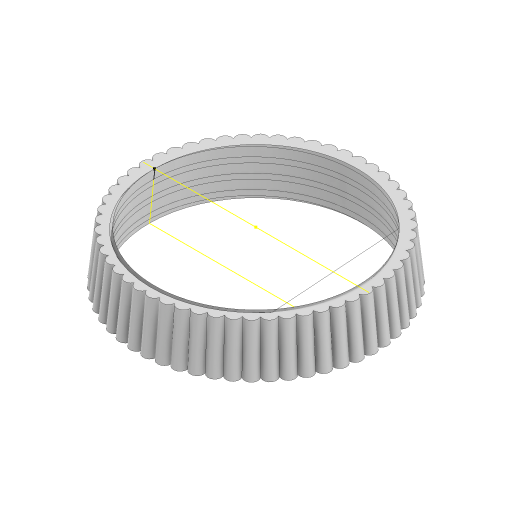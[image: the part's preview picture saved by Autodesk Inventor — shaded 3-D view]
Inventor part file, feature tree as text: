
AUTODESK INVENTOR PART (.ipt)
format: ipt  version: 2023 (Build 270158000, 158)  size: 462,336 bytes
history: native  units: mm
features: sketch x5, draft x2, helix x2, extrude x1, sweep x1, pattern_circular x1
ambient origin geometry x8: Origin, YZ Plane, XZ Plane, XY Plane, X Axis, Y Axis, Z Axis, Center Point
bodies: Solid1 (feature_tree)
feature tree (12):
  extrude  "Extrusion1"  Depth=6.52mm TaperAngle=0.0deg
  draft  "FaceDraft1"
  sketch  "Sketch2"  dims[d7=2.0mm d8=9.0mm d9=10.0mm d10=1.047198mm d11=90.0deg d12=90.0deg d13=0.0mm d14=0.0mm d15=2.0mm d16=3.0mm d17=10.0mm d18=-1.047198mm d19=90.0deg d20=90.0deg d21=0.0mm d22=0.0mm d23=1.5mm d91=1.047198mm]
  sketch  "Sketch4"  dims[d93=1.75mm d95=0.0mm d96=0.0mm d97=540.0mm d98=360.0deg]
  helix  "Coil1"  [1 undecoded]
  helix  "Coil2"  [1 undecoded]
  draft  "FaceDraft2"
  sweep  "Sweep1"
  pattern_circular  "Circular Pattern3"  Count=54 Angle=360.0deg
  sketch  "Sketch1"  dims[d0=26.5mm d2=6.52mm d3=0.0mm d4=1.047198mm]
  sketch  "Sketch9"
  sketch  "Sketch10"
note: 2 required parameter values undecoded (feature->parameter linkage not recoverable at this tier; creation-order binding heuristic only, values carry confidence <= 0.55)
